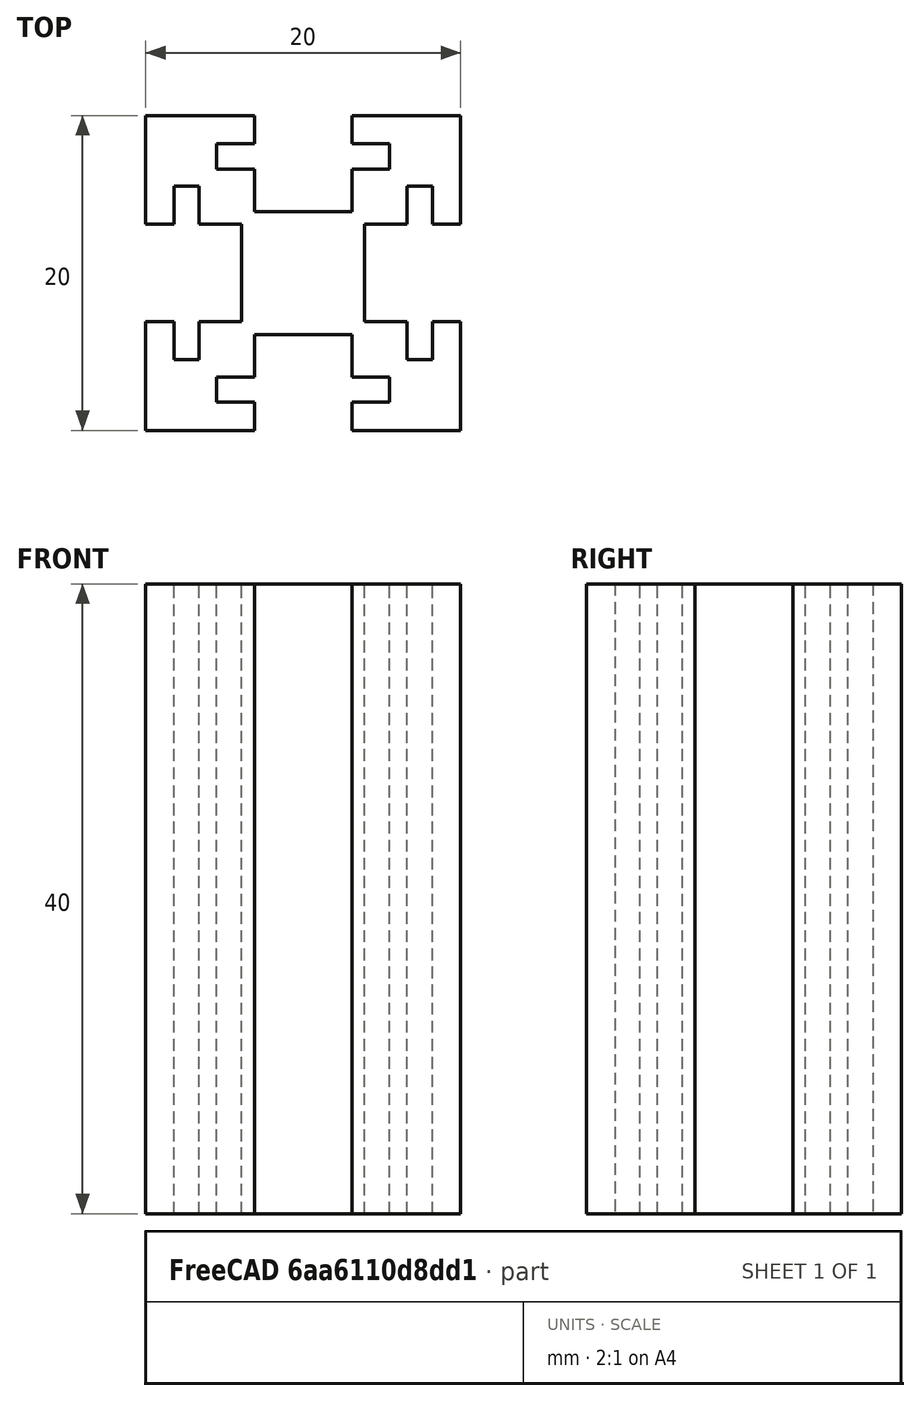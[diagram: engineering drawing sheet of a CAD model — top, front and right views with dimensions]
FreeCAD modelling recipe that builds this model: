
FCSTD DOCUMENT  (FreeCAD 0.17R13522 (Git))
Label: primeiroTeste
License: All rights reserved
LicenseURL: http://en.wikipedia.org/wiki/All_rights_reserved
objects: Part::Box×9, Part::Cut×8, App::MeasureDistance×1
note: 17 computed .brp shape members not serialized (recipe doc carries the construction recipe); baked Part::Feature solids carry a one-line shape summary decoded from their .brp

FEATURE [Part::Box] Box  label="Cube"
  AttacherType = Attacher::AttachEngine3D
  Height = 40
  Length = 20
  Width = 20
FEATURE [Part::Box] Box001  label="cortador"
  AttacherType = Attacher::AttachEngine3D
  Height = 52
  Length = 1.6
  Placement = pos=(1.8,4.5,-2) rot=(0,0,1;0rad)
  Width = 11
FEATURE [Part::Cut] Cut
  Base = -> Box
  Placement = pos=(0,0,-3) rot=(0,0,1;0rad)
  Tool = -> Box001
FEATURE [Part::Box] Box002  label="Cube001"
  AttacherType = Attacher::AttachEngine3D
  Height = 50
  Length = 1.6
  Placement = pos=(16.6,4.5,-6) rot=(0,0,1;0rad)
  Width = 11
FEATURE [Part::Box] Box004  label="Cube003"
  AttacherType = Attacher::AttachEngine3D
  Height = 50
  Length = 11
  Placement = pos=(4.5,1.8,-3) rot=(0,0,1;0rad)
  Width = 1.6
FEATURE [Part::Cut] Cut001
  Base = -> Cut
  Tool = -> Box002
FEATURE [Part::Box] Box005  label="Cube004"
  AttacherType = Attacher::AttachEngine3D
  Height = 50
  Length = 11
  Placement = pos=(4.5,16.6,-6) rot=(0,0,1;0rad)
  Width = 1.6
FEATURE [Part::Box] Box006  label="Cube005"
  AttacherType = Attacher::AttachEngine3D
  Height = 50
  Length = 6.1
  Placement = pos=(0,6.9,-7) rot=(0,0,1;0rad)
  Width = 6.2
FEATURE [Part::Box] Box007  label="Cube006"
  AttacherType = Attacher::AttachEngine3D
  Height = 50
  Length = 6.1
  Placement = pos=(13.9,6.9,-7) rot=(0,0,1;0rad)
  Width = 6.2
FEATURE [Part::Box] Box009  label="Cube008"
  AttacherType = Attacher::AttachEngine3D
  Height = 50
  Length = 6.2
  Placement = pos=(6.9,0,-7) rot=(0,0,1;0rad)
  Width = 6.1
FEATURE [Part::Cut] Cut002
  Base = -> Cut001
  Tool = -> Box004
FEATURE [Part::Cut] Cut003
  Base = -> Cut002
  Tool = -> Box005
FEATURE [Part::Cut] Cut004
  Base = -> Cut003
  Tool = -> Box006
FEATURE [Part::Cut] Cut005
  Base = -> Cut004
  Tool = -> Box007
FEATURE [Part::Box] Box010  label="Cube009"
  AttacherType = Attacher::AttachEngine3D
  Height = 50
  Length = 6.2
  Placement = pos=(6.9,13.9,-7) rot=(0,0,1;0rad)
  Width = 6.1
FEATURE [Part::Cut] Cut006
  Base = -> Cut005
  Tool = -> Box009
FEATURE [Part::Cut] Cut007
  Base = -> Cut006
  Tool = -> Box010
FEATURE [App::MeasureDistance] Distance  label="Distance: 1,58 mm"
  Distance = 1.58366
  P1 = (3.4285,15.5017,37)
  P2 = (4.56939,16.6,37)
